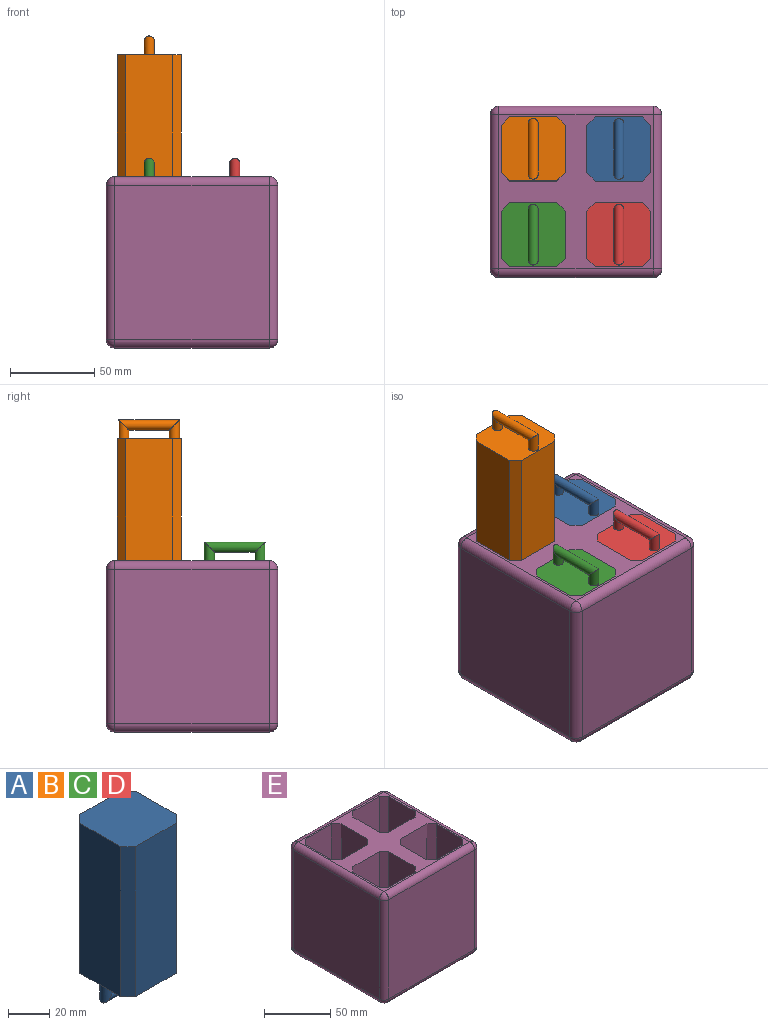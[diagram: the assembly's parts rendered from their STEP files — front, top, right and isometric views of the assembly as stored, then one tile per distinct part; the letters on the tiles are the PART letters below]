
ASSEMBLY  parts=5 mates=6
PART A: 47 faces, bbox 38.1x38.1x99.9 mm
  f0: plane 38.1x38.1mm, normal (0,0,-1), area 1343.4mm2, adj f1,f2,f3,f4,f16,f17,f18,f19
  f1: plane 88.9x27.94mm, normal (1,0,0), area 592.7mm2, adj f0,f5,f6,f7,f8,f9,f11,f12
  f2: plane 88.9x27.94mm, normal (0,1,0), area 2483.9mm2, adj f0,f5,f16,f17
  f3: plane 88.9x27.94mm, normal (-1,0,0), area 2483.9mm2, adj f0,f5,f16,f18
  f4: plane 88.9x27.94mm, normal (0,-1,0), area 2483.9mm2, adj f0,f5,f18,f19
  f5: plane 38.1x38.1mm, normal (0,0,1), area 1400mm2, adj f1,f2,f3,f4,f16,f17,f18,f19
  f6: plane 20.32x15.24mm, normal (0,0,1), area 309.7mm2, adj f1,f22,f28,f31
  f7: plane 27.94x20.32mm, normal (0,-1,0), area 567.7mm2, adj f1,f25,f29,f31
  f8: plane 20.32x15.24mm, normal (0,0,-1), area 309.7mm2, adj f1,f20,f24,f25
  f9: plane 27.94x20.32mm, normal (0,1,0), area 567.7mm2, adj f1,f20,f22,f23
  f10: plane 27.94x15.24mm, normal (1,0,0), area 425.8mm2, adj f23,f24,f28,f29
  f11: plane 20.32x15.24mm, normal (0,0,1), area 309.7mm2, adj f1,f37,f41,f43
  f12: plane 27.94x20.32mm, normal (0,-1,0), area 567.7mm2, adj f1,f32,f36,f37
  f13: plane 20.32x15.24mm, normal (0,0,-1), area 309.7mm2, adj f1,f32,f34,f35
  f14: plane 27.94x20.32mm, normal (0,1,0), area 567.7mm2, adj f1,f34,f40,f43
  f15: plane 27.94x15.24mm, normal (1,0,0), area 425.8mm2, adj f35,f36,f40,f41
  f16: plane 88.9x5.08mm, normal (-0.71,0.71,0), area 638.7mm2, adj f0,f2,f3,f5
  f17: plane 88.9x5.08mm, normal (0.71,0.71,0), area 638.7mm2, adj f0,f1,f2,f5
  f18: plane 88.9x5.08mm, normal (-0.71,-0.71,0), area 638.7mm2, adj f0,f3,f4,f5
  f19: plane 88.9x5.08mm, normal (0.71,-0.71,0), area 638.7mm2, adj f0,f1,f4,f5
  f20: cylinder r=5.08mm len=20.32mm, axis (1,0,0), area 162.1mm2, adj f1,f8,f9,f21
  f21: sphere r=5.08mm, area 40.5mm2, adj f20,f23,f24
  f22: cylinder r=5.08mm len=20.32mm, axis (-1,0,0), area 162.1mm2, adj f1,f6,f9,f26
  f23: cylinder r=5.08mm len=27.94mm, axis (0,0,-1), area 223mm2, adj f9,f10,f21,f26
  f24: cylinder r=5.08mm len=15.24mm, axis (0,-1,0), area 121.6mm2, adj f8,f10,f21,f27
  f25: cylinder r=5.08mm len=20.32mm, axis (-1,0,0), area 162.1mm2, adj f1,f7,f8,f27
  f26: sphere r=5.08mm, area 42.8mm2, adj f22,f23,f28
  f27: sphere r=5.08mm, area 40.5mm2, adj f24,f25,f29
  f28: cylinder r=5.08mm len=15.24mm, axis (0,1,0), area 121.6mm2, adj f6,f10,f26,f30
  f29: cylinder r=5.08mm len=27.94mm, axis (0,0,1), area 223mm2, adj f7,f10,f27,f30
  f30: sphere r=5.08mm, area 40.5mm2, adj f28,f29,f31
  f31: cylinder r=5.08mm len=20.32mm, axis (1,0,0), area 162.1mm2, adj f1,f6,f7,f30
  f32: cylinder r=5.08mm len=20.32mm, axis (-1,0,0), area 162.1mm2, adj f1,f12,f13,f33
  f33: sphere r=5.08mm, area 40.5mm2, adj f32,f35,f36
  f34: cylinder r=5.08mm len=20.32mm, axis (1,0,0), area 162.1mm2, adj f1,f13,f14,f38
  f35: cylinder r=5.08mm len=15.24mm, axis (0,-1,0), area 121.6mm2, adj f13,f15,f33,f38
  f36: cylinder r=5.08mm len=27.94mm, axis (0,0,1), area 223mm2, adj f12,f15,f33,f39
  f37: cylinder r=5.08mm len=20.32mm, axis (1,0,0), area 162.1mm2, adj f1,f11,f12,f39
  f38: sphere r=5.08mm, area 40.5mm2, adj f34,f35,f40
  f39: sphere r=5.08mm, area 40.5mm2, adj f36,f37,f41
  f40: cylinder r=5.08mm len=27.94mm, axis (0,0,-1), area 223mm2, adj f14,f15,f38,f42
  f41: cylinder r=5.08mm len=15.24mm, axis (0,1,0), area 121.6mm2, adj f11,f15,f39,f42
  f42: sphere r=5.08mm, area 40.5mm2, adj f40,f41,f43
  f43: cylinder r=5.08mm len=20.32mm, axis (-1,0,0), area 162.1mm2, adj f1,f11,f14,f42
  f44: cylinder r=3mm len=11mm, axis (0,0,1), area 150.8mm2, adj f0,f45
  f45: cylinder r=3mm len=36mm, axis (-1,0,0), area 565.5mm2, adj f44,f46
  f46: cylinder r=3mm len=11mm, axis (0,0,-1), area 150.8mm2, adj f0,f45
PART B: same geometry as A
PART C: same geometry as A
PART D: same geometry as A
PART E: 62 faces, bbox 101.6x101.6x101.6 mm
  f0: plane 91.44x91.44mm, normal (0,0,1), area 2761.3mm2, adj f6,f7,f8,f9,f11,f12,f13,f14
  f1: plane 91.44x91.44mm, normal (0,1,0), area 8361.3mm2, adj f31,f35,f37,f55
  f2: plane 91.44x91.44mm, normal (-1,0,0), area 8361.3mm2, adj f28,f34,f37,f59
  f3: plane 91.44x91.44mm, normal (0,-1,0), area 8361.3mm2, adj f26,f28,f29,f60
  f4: plane 91.44x91.44mm, normal (1,0,0), area 8361.3mm2, adj f26,f30,f31,f56
  f5: plane 91.44x91.44mm, normal (0,0,-1), area 8361.3mm2, adj f29,f30,f34,f35
  f6: plane 88.9x27.94mm, normal (0,1,0), area 2483.9mm2, adj f0,f10,f43,f47
  f7: plane 88.9x27.94mm, normal (-1,0,0), area 2483.9mm2, adj f0,f10,f38,f43
  f8: plane 88.9x27.94mm, normal (0,-1,0), area 2483.9mm2, adj f0,f10,f38,f46
  f9: plane 88.9x27.94mm, normal (1,0,0), area 2483.9mm2, adj f0,f10,f46,f47
  f10: plane 38.1x38.1mm, normal (0,0,1), area 1400mm2, adj f6,f7,f8,f9,f38,f43,f46,f47
  f11: plane 88.9x27.94mm, normal (-1,0,0), area 2483.9mm2, adj f0,f15,f40,f42
  f12: plane 88.9x27.94mm, normal (0,-1,0), area 2483.9mm2, adj f0,f15,f40,f45
  f13: plane 88.9x27.94mm, normal (1,0,0), area 2483.9mm2, adj f0,f15,f45,f48
  f14: plane 88.9x27.94mm, normal (0,1,0), area 2483.9mm2, adj f0,f15,f42,f48
  f15: plane 38.1x38.1mm, normal (0,0,1), area 1400mm2, adj f11,f12,f13,f14,f40,f42,f45,f48
  f16: plane 88.9x27.94mm, normal (0,-1,0), area 2483.9mm2, adj f0,f20,f39,f44
  f17: plane 88.9x27.94mm, normal (1,0,0), area 2483.9mm2, adj f0,f20,f44,f49
  f18: plane 88.9x27.94mm, normal (0,1,0), area 2483.9mm2, adj f0,f20,f41,f49
  f19: plane 88.9x27.94mm, normal (-1,0,0), area 2483.9mm2, adj f0,f20,f39,f41
  f20: plane 38.1x38.1mm, normal (0,0,1), area 1400mm2, adj f16,f17,f18,f19,f39,f41,f44,f49
  f21: plane 88.9x27.94mm, normal (1,0,0), area 2483.9mm2, adj f0,f25,f50,f51
  f22: plane 88.9x27.94mm, normal (0,1,0), area 2483.9mm2, adj f0,f25,f50,f52
  f23: plane 88.9x27.94mm, normal (-1,0,0), area 2483.9mm2, adj f0,f25,f52,f53
  f24: plane 88.9x27.94mm, normal (0,-1,0), area 2483.9mm2, adj f0,f25,f51,f53
  f25: plane 38.1x38.1mm, normal (0,0,1), area 1400mm2, adj f21,f22,f23,f24,f50,f51,f52,f53
  f26: cylinder r=5.08mm len=91.44mm, axis (0,0,1), area 729.7mm2, adj f3,f4,f27,f58
  f27: sphere r=5.08mm, area 40.5mm2, adj f26,f29,f30
  f28: cylinder r=5.08mm len=91.44mm, axis (0,0,-1), area 729.7mm2, adj f2,f3,f32,f61
  f29: cylinder r=5.08mm len=91.44mm, axis (1,0,0), area 729.7mm2, adj f3,f5,f27,f32
  f30: cylinder r=5.08mm len=91.44mm, axis (0,1,0), area 729.7mm2, adj f4,f5,f27,f33
  f31: cylinder r=5.08mm len=91.44mm, axis (0,0,-1), area 729.7mm2, adj f1,f4,f33,f54
  f32: sphere r=5.08mm, area 40.5mm2, adj f28,f29,f34
  f33: sphere r=5.08mm, area 40.5mm2, adj f30,f31,f35
  f34: cylinder r=5.08mm len=91.44mm, axis (0,-1,0), area 729.7mm2, adj f2,f5,f32,f36
  f35: cylinder r=5.08mm len=91.44mm, axis (-1,0,0), area 729.7mm2, adj f1,f5,f33,f36
  f36: sphere r=5.08mm, area 40.5mm2, adj f34,f35,f37
  f37: cylinder r=5.08mm len=91.44mm, axis (0,0,1), area 729.7mm2, adj f1,f2,f36,f57
  f38: plane 88.9x5.08mm, normal (-0.71,-0.71,0), area 638.7mm2, adj f0,f7,f8,f10
  f39: plane 88.9x5.08mm, normal (-0.71,-0.71,0), area 638.7mm2, adj f0,f16,f19,f20
  f40: plane 88.9x5.08mm, normal (-0.71,-0.71,0), area 638.7mm2, adj f0,f11,f12,f15
  f41: plane 88.9x5.08mm, normal (-0.71,0.71,0), area 638.7mm2, adj f0,f18,f19,f20
  f42: plane 88.9x5.08mm, normal (-0.71,0.71,0), area 638.7mm2, adj f0,f11,f14,f15
  f43: plane 88.9x5.08mm, normal (-0.71,0.71,0), area 638.7mm2, adj f0,f6,f7,f10
  f44: plane 88.9x5.08mm, normal (0.71,-0.71,0), area 638.7mm2, adj f0,f16,f17,f20
  f45: plane 88.9x5.08mm, normal (0.71,-0.71,0), area 638.7mm2, adj f0,f12,f13,f15
  f46: plane 88.9x5.08mm, normal (0.71,-0.71,0), area 638.7mm2, adj f0,f8,f9,f10
  f47: plane 88.9x5.08mm, normal (0.71,0.71,0), area 638.7mm2, adj f0,f6,f9,f10
  f48: plane 88.9x5.08mm, normal (0.71,0.71,0), area 638.7mm2, adj f0,f13,f14,f15
  f49: plane 88.9x5.08mm, normal (0.71,0.71,0), area 638.7mm2, adj f0,f17,f18,f20
  f50: plane 88.9x5.08mm, normal (0.71,0.71,0), area 638.7mm2, adj f0,f21,f22,f25
  f51: plane 88.9x5.08mm, normal (0.71,-0.71,0), area 638.7mm2, adj f0,f21,f24,f25
  f52: plane 88.9x5.08mm, normal (-0.71,0.71,0), area 638.7mm2, adj f0,f22,f23,f25
  f53: plane 88.9x5.08mm, normal (-0.71,-0.71,0), area 638.7mm2, adj f0,f23,f24,f25
  f54: sphere r=5.08mm, area 40.5mm2, adj f31,f55,f56
  f55: cylinder r=5.08mm len=91.44mm, axis (1,0,0), area 729.7mm2, adj f0,f1,f54,f57
  f56: cylinder r=5.08mm len=91.44mm, axis (0,-1,0), area 729.7mm2, adj f0,f4,f54,f58
  f57: sphere r=5.08mm, area 40.5mm2, adj f37,f55,f59
  f58: sphere r=5.08mm, area 40.5mm2, adj f26,f56,f60
  f59: cylinder r=5.08mm len=91.44mm, axis (0,1,0), area 729.7mm2, adj f0,f2,f57,f61
  f60: cylinder r=5.08mm len=91.44mm, axis (-1,0,0), area 729.7mm2, adj f0,f3,f58,f61
  f61: sphere r=5.08mm, area 40.5mm2, adj f28,f59,f60
PLACE A rot(axis=(0.71,0.71,0),180deg) t=(44.37,49.16,105.58)mm
PLACE B rot(axis=(0.71,0.71,0),180deg) t=(-6.43,49.16,178.03)mm
PLACE C rot(axis=(0.71,0.71,0),180deg) t=(-6.43,-1.64,105.58)mm
PLACE D rot(axis=(0.71,0.71,0),180deg) t=(44.37,-1.64,105.58)mm
PLACE E t=(18.97,23.76,3.98)mm fixed
MATE planar D.f2 <-> E.f19  axis (1,0,0) through (63.42,-1.64,61.13)mm
MATE planar B.f4 <-> E.f9  axis (-1,0,0) through (-25.48,49.16,133.58)mm
MATE planar B.f2 <-> E.f7  axis (1,0,0) through (12.62,49.16,133.58)mm
MATE planar C.f3 <-> E.f14  axis (0,-1,0) through (-6.43,-20.69,61.13)mm
MATE planar B.f3 <-> E.f6  axis (0,-1,0) through (-6.43,30.11,133.58)mm
MATE planar A.f2 <-> E.f23  axis (1,0,0) through (63.42,49.16,61.13)mm
